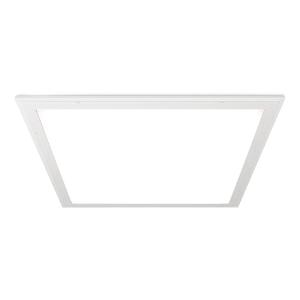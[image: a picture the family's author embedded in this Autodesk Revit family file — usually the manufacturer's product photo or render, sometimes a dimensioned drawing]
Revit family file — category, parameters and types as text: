
# Revit family: 3f_filippi_-_l_650_luce_diffusa_vss_3f_filippi_-_21896_-_l_650_52w-940_dali_vss_599x599
name_source: partatom
category: Lighting Fixtures
units: mm (PartAtom-declared; Revit-internal decimal feet)

## family parameters
Cut with Voids When Loaded = No
Host = Face
Light Source = No
Part Type = Normal
Room Calculation Point = No
Round Connector Dimension = Use Diameter
Shared = No

## types (1)
- 3F Filippi - L 650 Luce Diffusa VSS (1 x LED, 5023 lm, 57 W, 4000 K)
    Apparent Load = 57 VA
    Approval mark = ENEC
    CIE Flux Codes = 63 92 98 100 100
    Color Rendering = 90
    Color Temperature = 4000 K
    Control Gear = Electronic transformer
    Default Elevation = 1800 mm
    Description = ILLUMINOTECHNICAL
Luminous efficiency 100% (DLOR 100%, ULOR 0%).
Initial luminous flux of the luminaire 5023 lm.
Direct symmetric distribution.
Installation Interdistance Transv.D = 1.17 x hu - Long.D = 1.16 x hu.
Average luminance <3000 cd/m² for radial angles >65°.
Tabular UGR (CIE 117 - 4H-8H; S=0.25H; 70/50/20): RUG 18 - 17.9.
Beam angle: 90° - 88°.
Luminous efficacy 88 lm/W.
Lifetime (L93/B10): 30000 h. (tq+25°C)
Lifetime (L90/B10): 50000 h. (tq+25°C)
Lifetime (L85/B10): 80000 h. (tq+25°C)
Lifetime (L80/B10): 100000 h. (tq+25°C)
Sudden decreased luminous flux after 50000 hours: 0% (C0).
Photobiological safety in compliance with IEC/TR 62778: RG0 risk exempt, (IEC 62471).
In compliance with IEC/EN 62722-2-1 - IEC/EN 62717 standards.

SOURCE
Squared LED module 52W/940.
Source with special protection against aggressive chemically-volatile substances for standard LED technology.
Energy efficiency class (UE 2019/2020 - UE 2019/2015): E.
CIE 13.3 Colour rendering index: CRI >90 (R9 >50%).
IES TM-30 Fidelity Index: Rf = 92 Rg = 101.
CCT nominal colour temperature 4000 K.
Colour initial tolerance (MacAdam): SDCM 3.

MECHANICAL
Housing in galvannealed steel, painted in white epoxy-polyester.
Perimetral frame in white stainless steel.
VSS moulded laminated dipped glass, non-combustible, thickness 7 mm.
Anti-glare opal polycarbonate filter for brightness uniformity.
The version 599x599 is dedicated to modular metal false ceilings with dimensions of 600x600.
Luminaire with limited surface temperature. - D - (EN 60598-2-24)
Dimensions: 599x599 mm, height 90 mm. Weight 10.66 kg.
IP66 protection degree for exposed part, IP64 for recessed part.
Mechanical strength to impacts IK08 (5 joule).
Glow-wire test resistance 650°C.

ELECTRICAL
Halogen Free DALI-2 DATI (Parts 251, 252, 253), PUSH-DIM, electronic wiring 230V-50/60Hz, power factor 0.95 at full load, THD <25%, constant output current, SELV, class I, 1 driver, 1 DALI addresse.
Power of the luminaire 57 W.
CE - IEC 60598-1 - EN 60598-1.
SAFE FLICKER: PstLM=<1 and SVM=<0.4 (IEC TR 61547-1 and IEC TR 63158), to ensure a more comfortable and safe light.
Luminaire compliant with EN 60598-2-22 for power supply from a centralised emergency system CPSS (Central Power Supply System), not incorporated in the luminaire - high risk areas excluded. The default power and flux are 100% in AC and 15% in DC.
Ambient temperature from 0°C to +40°C.
Temperature class T6 max 85°C.
5-pole terminal block (L-N-PE-DA/DA) quick connection for line connection with connection capacity 2x2.5 mm² per poles.
Relative humidity UR: <85%.

INSTALLATION
Trimless recessed fitting, to be used with inspectable false-ceilings that can be inspected using fixing brackets which are always required, also designed for the hanging from rough ceiling.
All accessories dedicated to this product are available on the Catalog and on our website www.3F-Filippi.com.

APPLICATIONS
Suitable product for food production plants (HACCP), IFS (Food Version 6), BRC (GSFS Food Version 7).
Environments: hospital premises, transit areas, laboratories, platform-roof, underpasses.
Environments: sterilized, aseptic.
In hospital environments, food industry or machines with parts in motion, with considerable sudden temperature changes, and in general in any environments requiring total protection against falling fragments, use luminaires with laminated glass only.
Tempered glass is not immune to falling fragments from harmless and caused by shocks or exceptionally derived from the tempering process.
Environments requiring a high level of protection and simplified cleaning.
Environments with exacting visual tasks, where diffused soft light for optimum visual comfort is required.

LIGHT MANAGEMENT
Recommended minimum setting: 10%.
The luminaire, equipped with (DALI-2 DATI) driver, can be controlled manually with 3F Easy Dim technology or automatically/manually with wired or wireless DALI/D2D control systems.
The D2D driver guarantees interoperability with other devices with the same certification by making the following information available:
Device Data (Part 251), Energy Report (Part 252), Diagnosis & Maintenance (Part 253).
In electrical systems without a regulation system (manual or automatic) and DALI bus, a suitable jumper must be made on the DA-DA terminals of the appliance.

WARNING
Luminaire designed for disposal/recycling at end-of-life.
Replaceable (LED only) light source by a professional. Replaceable control gear by a professional.
    Height = 0 mm  [stored 0 ft]
    Lamp = 1 x LED
    Lamp Light Flux = 5023 lm
    Lamp Power = 57 W
    Lamp count = 1
    Length = 599 mm
    Lifetime = 50000 h
    Luminous efficacy = 88 lm/W
    Manufacturer = 3F Filippi
    ModVariant = No
    Model = 3F Filippi - 21896 - L 650 52W-940 DALI VSS 599x599
    Mounting Place = Ceiling
    Mounting Type = Recessed
    Number of Poles = 1
    OnlyDefault = Yes
    Power Factor = 1
    Product Name = 3F Filippi - L 650 Luce Diffusa VSS
    Product group = recessed luminaire
    ProductGroupID = 4
    Protection Class = Protection class I
    Protection Degree = IP 64
    RLX_Detail_Level = 1
    RLX_Emergency_Light_Flux = 0 lm
    RLX_Emergency_Type = 0
    RLX_Emergency_Type_DB = No
    RlxData = <blob elided: 100985 chars, md5=490884d1>
    Socket = socket
    Standby Power = 0 W
    System Light Flux = 5023 lm
    System Power = 57 W
    Type Comments = Product without accessories
    Type Image = 3ffilippi_l_650_luce_diffusa_vss.jpg
    URL = http://relux.com
    VarID = ---
    Voltage = 0 V
    Weight = 0.00 kg
    Width = 599 mm

note: [stored X ft] marks values corroborated as IEEE doubles in the binary element streams (Revit-internal decimal feet)

## geometry (parser evidence)
native form markers: Blend x4, Sweep x9
no freeform markers — native parametric forms only
